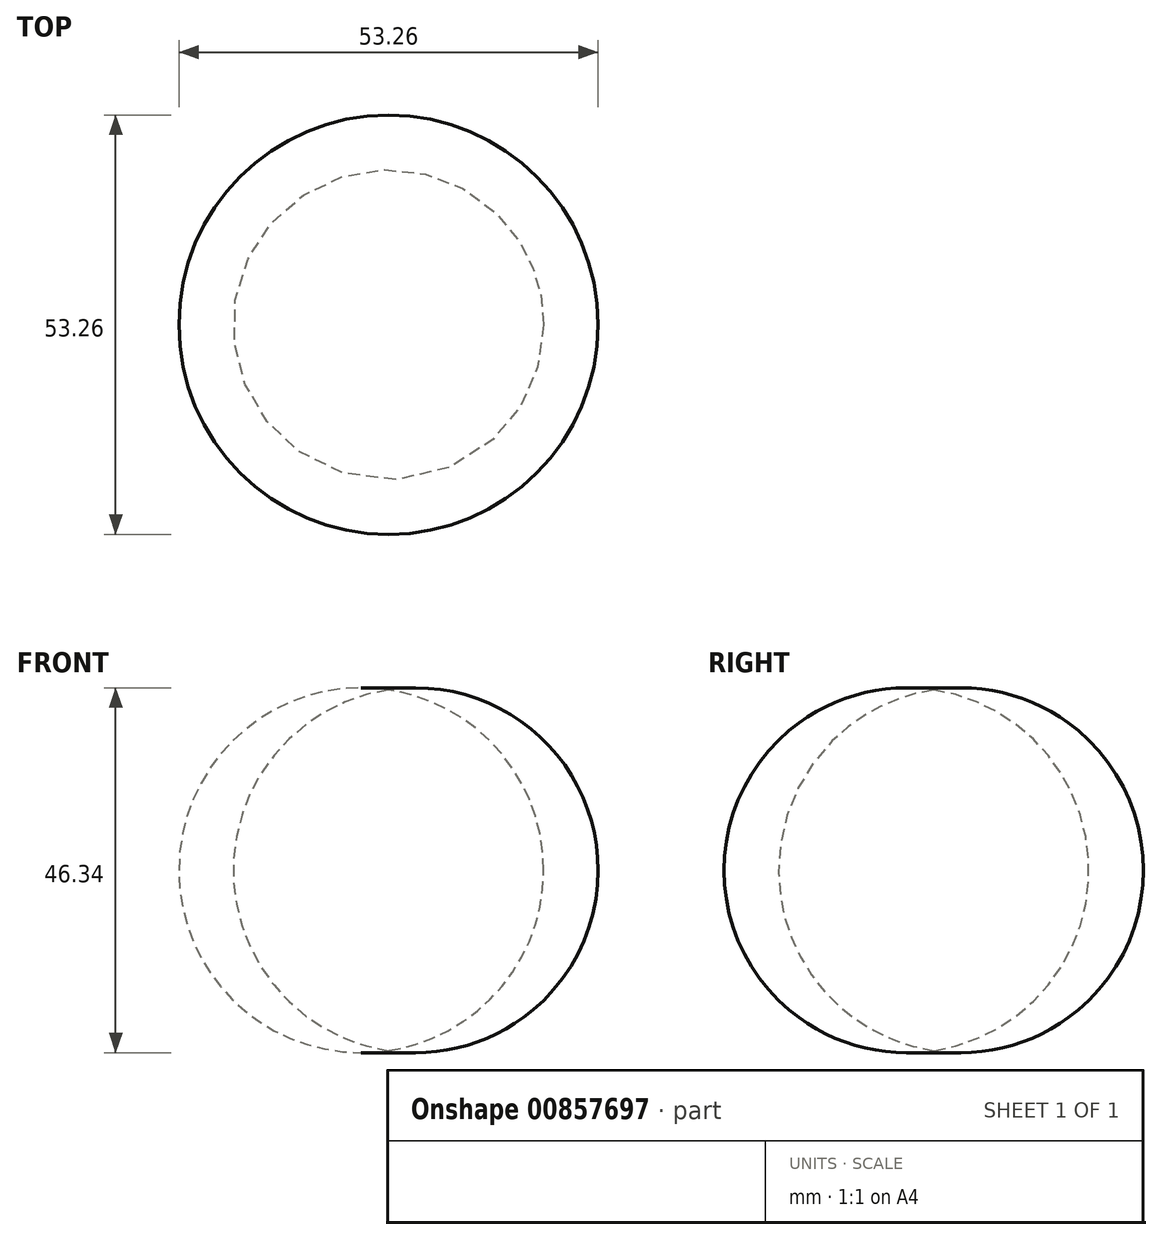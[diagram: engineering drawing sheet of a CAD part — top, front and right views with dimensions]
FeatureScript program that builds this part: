
annotation { "Feature Type Name" : "Feature", "Feature Type Description" : "" }
export const myFeature = defineFeature(function(context is Context, id is Id, definition is map)
    precondition{}
    {
        {
            var Q0;
            Q0=qCreatedBy(makeId("Front.planeOp"),FACE);
            var sketch = newSketch(context, id + "F0", { "sketchPlane" : qUnion([Q0])});
            skLineSegment(sketch, "E0", {"start": v(0, 0) * mm, "end": v(0, 38.1) * mm});
            skArc(sketch, "E1", {"start": v(0, 0) * mm, "mid": v(22.82, 19.05) * mm, "end": v(0, 38.1) * mm});
            skArc(sketch, "E2.0", {"start": v(0, -3.86) * mm, "mid": v(26.63, 19.05) * mm, "end": v(0, 41.96) * mm});
            skLineSegment(sketch, "E3", {"start": v(0, 41.96) * mm, "end": v(0, 38.1) * mm});
            skLineSegment(sketch, "E4", {"start": v(0, -3.86) * mm, "end": v(0, 0) * mm});
            skLineSegment(sketch, "E5", {"start": v(0, 0) * mm, "end": v(0, 65.52) * mm});
            skSolve(sketch);
        }
        {
            var Q0;
            {var subQ0=sQuery(id+"F0.wireOp",EDGE,"E1");Q0=makeQuery(id+"F0.imprint","IMPRINT",FACE,{"disambiguationData":[TD([[makeQuery(id+"F0.imprint","IMPRINT",EDGE,{"derivedFrom":subQ0}),-1.0]])]});}
            var Q1;
            {var subQ0=sQuery(id+"F0.wireOp",EDGE,"E1");Q1=makeQuery(id+"F0.imprint","IMPRINT",FACE,{"disambiguationData":[TD([[makeQuery(id+"F0.imprint","IMPRINT",EDGE,{"derivedFrom":subQ0}),1.0]])]});}
            var Q2;
            Q2=sQuery(id+"F0.wireOp",EDGE,"E5");
            revolve(context, id + "F1", {"surfaceOperationType" : NewSurfaceOperationType.NEW, "entities" : qUnion([Q0, Q1]), "axis" : qUnion([Q2]), "revolveType" : RevolveType.FULL});
        }
    });
